annotation { "Feature Type Name" : "Feature", "Feature Type Description" : "" }
export const myFeature = defineFeature(function(context is Context, id is Id, definition is map)
    precondition{}
    {
        {
            var Q0;
            Q0=qCreatedBy(makeId("Right.planeOp"),FACE);
            var sketch = newSketch(context, id + "F0", { "sketchPlane" : qUnion([Q0])});
            skLineSegment(sketch, "E0", {"start": v(-21.82, 0) * mm, "end": v(-21.68, 0.07) * mm});
            skLineSegment(sketch, "E1", {"start": v(41.62, 29.58) * mm, "end": v(41.62, 0) * mm});
            skLineSegment(sketch, "E2", {"start": v(41.62, 0) * mm, "end": v(-21.82, 0) * mm});
            skLineSegment(sketch, "E3", {"start": v(-21.68, 0.07) * mm, "end": v(-25.7, 8.7) * mm});
            skLineSegment(sketch, "E4", {"start": v(-25.7, 8.7) * mm, "end": v(-22.1, 10.38) * mm});
            skLineSegment(sketch, "E5", {"start": v(-22.1, 10.38) * mm, "end": v(-18.08, 1.75) * mm});
            skLineSegment(sketch, "E6.trimOffspring", {"start": v(-18.08, 1.75) * mm, "end": v(41.62, 29.58) * mm});
            skSolve(sketch);
        }
        {
            var Q0;
            Q0 = qSketchRegion(id + "F0", true);
            extrude(context, id + "F1", {"entities" : qUnion([Q0]), "depth" : 101.6 * mm, "offsetDistance" : 25.4 * mm});
        }
        {
            var Q0;
            Q0=makeQuery(id+"F1.opExtrude","SWEPT_FACE",FACE,{"disambiguationData":[OSD([sQuery(id+"F0.wireOp",EDGE,"E2")])]});
            var sketch = newSketch(context, id + "F2", { "sketchPlane" : qUnion([Q0])});
            skLineSegment(sketch, "E7.bottom", {"start": v(0, 21.82) * mm, "end": v(101.6, 21.82) * mm});
            skLineSegment(sketch, "E7.top", {"start": v(0, -41.62) * mm, "end": v(101.6, -41.62) * mm});
            skLineSegment(sketch, "E7.left", {"start": v(0, 21.82) * mm, "end": v(0, -41.62) * mm});
            skLineSegment(sketch, "E7.right", {"start": v(101.6, 21.82) * mm, "end": v(101.6, -41.62) * mm});
            skSolve(sketch);
        }
        {
            var Q0;
            Q0 = qSketchRegion(id + "F2", true);
            extrude(context, id + "F3", {"entities" : qUnion([Q0]), "operationType" : NewBodyOperationType.ADD, "depth" : 3 * mm, "offsetDistance" : 25.4 * mm});
        }
        {
            var Q0;
            Q0=makeQuery(id+"F3.boolean.opBoolean","MERGE",FACE,{"derivedFrom":[makeQuery(id+"F1.opExtrude","CAP_FACE",FACE,{"disambiguationData":[OSD([sQuery(id+"F0.wireOp",EDGE,"E0"),sQuery(id+"F0.wireOp",EDGE,"E1"),sQuery(id+"F0.wireOp",EDGE,"E2"),sQuery(id+"F0.wireOp",EDGE,"E3"),sQuery(id+"F0.wireOp",EDGE,"E4"),sQuery(id+"F0.wireOp",EDGE,"E5"),sQuery(id+"F0.wireOp",EDGE,"E6.trimOffspring")])],"isStart":false}),makeQuery(id+"F3.opExtrude","SWEPT_FACE",FACE,{"disambiguationData":[OSD([sQuery(id+"F2.wireOp",EDGE,"E7.right")])]})]});
            var sketch = newSketch(context, id + "F4", { "sketchPlane" : qUnion([Q0])});
            skLineSegment(sketch, "E8", {"start": v(-25.7, 8.7) * mm, "end": v(-19.24, -5.17) * mm});
            skLineSegment(sketch, "E9", {"start": v(-19.24, -5.17) * mm, "end": v(-28.28, -4.62) * mm});
            skLineSegment(sketch, "E10", {"start": v(-28.28, -4.62) * mm, "end": v(-25.7, 8.7) * mm});
            skSolve(sketch);
        }
        {
            var Q0;
            Q0 = qSketchRegion(id + "F4", true);
            extrude(context, id + "F5", {"entities" : qUnion([Q0]), "operationType" : NewBodyOperationType.REMOVE, "oppositeDirection" : true, "depth" : 129.54 * mm, "offsetDistance" : 25.4 * mm});
        }
        {
            var Q0;
            Q0=makeQuery(id+"F1.opExtrude","SWEPT_FACE",FACE,{"disambiguationData":[OSD([sQuery(id+"F0.wireOp",EDGE,"E6.trimOffspring")])]});
            var sketch = newSketch(context, id + "F6", { "sketchPlane" : qUnion([Q0])});
            skText(sketch, "E11", { "text": "PRAISE KEK", "fontName": "OpenSans-Bold.ttf"});
            const initialGuessF6  = {"E11": [0.00057, 0, 1, 0, 0.01294]};
            skSetInitialGuess(sketch, initialGuessF6);
            skSolve(sketch);
        }
        {
            var Q0;
            Q0 = qSketchRegion(id + "F6", true);
            extrude(context, id + "F7", {"entities" : qUnion([Q0]), "operationType" : NewBodyOperationType.REMOVE, "oppositeDirection" : true, "depth" : 1.66 * mm, "offsetDistance" : 25.4 * mm});
        }
    });